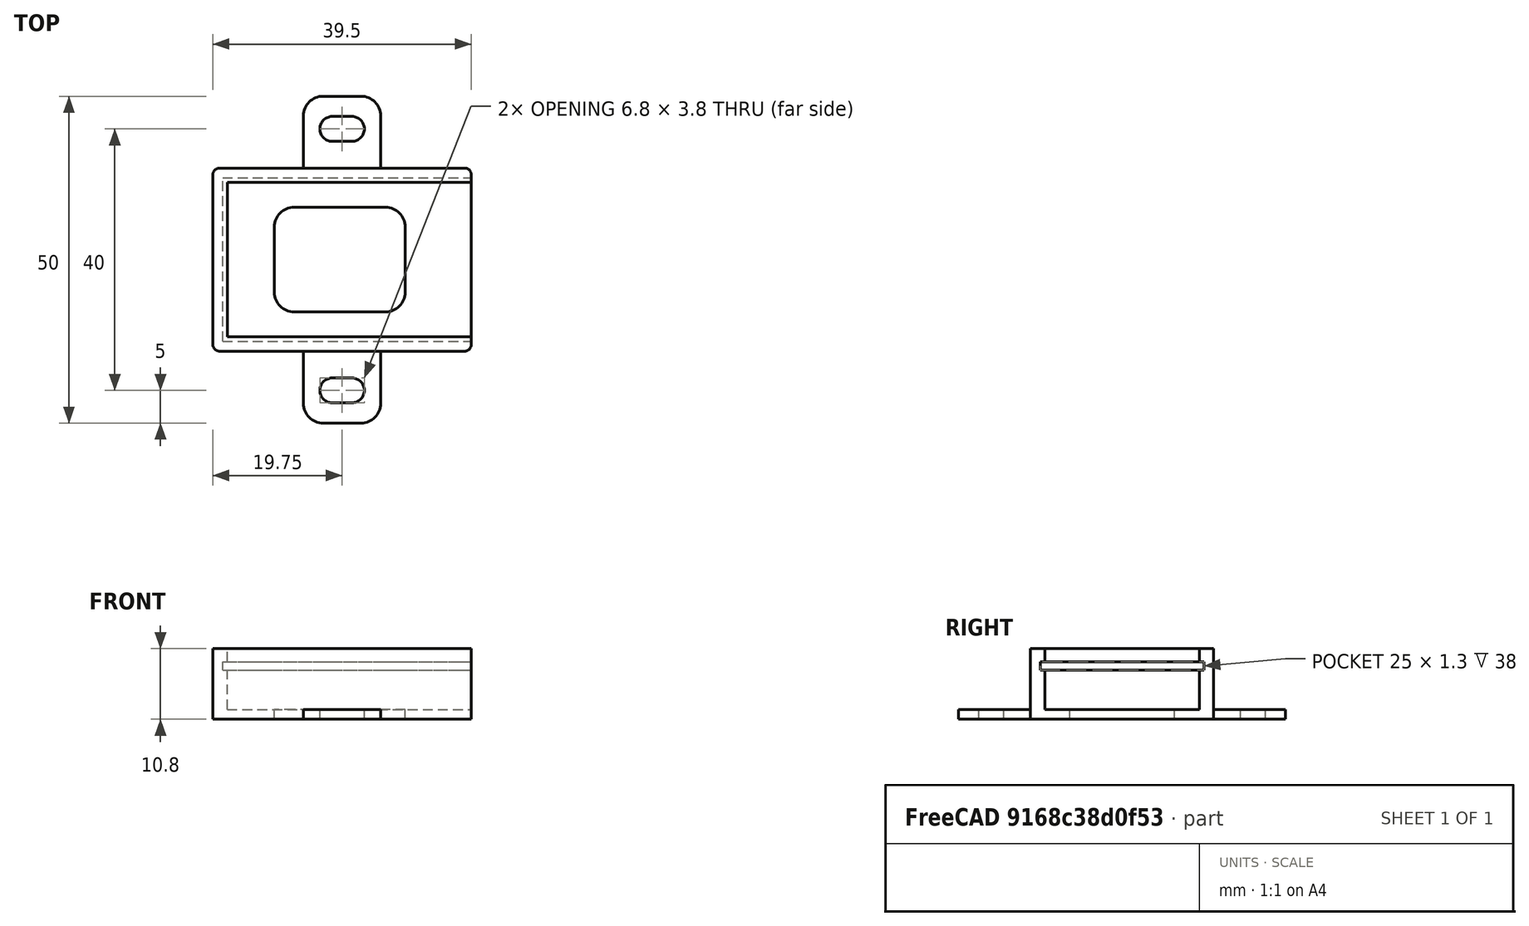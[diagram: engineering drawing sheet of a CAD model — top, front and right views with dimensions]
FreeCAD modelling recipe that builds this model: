
FCSTD DOCUMENT  (FreeCAD 0.19R23578 (Git))
Label: single_mosfet_30n06
License: FreeArt
LicenseURL: http://artlibre.org/licence/lal
objects: Part::Box×4, Part::Fillet×2, Part::MultiFuse×2, Spreadsheet::Sheet×1, Part::Feature×1, Part::Cut×1, App::Part×1
note: 10 computed .brp shape members not serialized (recipe doc carries the construction recipe); baked Part::Feature solids carry a one-line shape summary decoded from their .brp

FEATURE [Spreadsheet::Sheet] Spreadsheet  label="p"
  cells = A1=pcb_x; B1(pcb_x)=38; A2=pcb_y; B2(pcb_y)=25; A3=pcb_z; B3(pcb_z)=1.3; A4=pcb_under; B4(pcb_under)=6; A5=side_wall; B5(side_wall)=1.5; A6=pcb_side_lane; B6(pcb_side_lane)=0.7; A7=bottom_wall; B7(bottom_wall)=1.5; A8=pcb_above; B8(pcb_above)=2; A9=bottom_hole_x; B9(bottom_hole_x)=20; A10=bottom_hole_y; B10(bottom_hole_y)=16
FEATURE [Part::Box] Box  label="external cube"
  AttacherType = Attacher::AttachEngine3D
  Height = 10.8
  Length = 39.5
  Width = 28
  expr: Length = <<p>>.pcb_x + <<p>>.side_wall
  expr: Width = <<p>>.pcb_y + 2 * <<p>>.side_wall
  expr: Height = <<p>>.bottom_wall + <<p>>.pcb_under + <<p>>.pcb_z + <<p>>.pcb_above
FEATURE [Part::Box] Box006  label="internal cube"
  AttacherType = Attacher::AttachEngine3D
  Height = 9.3
  Length = 38.1
  Placement = pos=(2.2,2.2,1.5) rot=(0,0,1;0rad)
  Width = 23.6
  expr: Length = <<p>>.pcb_x - 2 * <<p>>.pcb_side_lane + <<p>>.side_wall
  expr: Width = <<p>>.pcb_y - 2 * <<p>>.pcb_side_lane
  expr: Height = <<p>>.pcb_under + <<p>>.pcb_z + <<p>>.pcb_above
  expr: .Placement.Base.z = <<p>>.bottom_wall
  expr: .Placement.Base.x = <<p>>.side_wall + <<p>>.pcb_side_lane
  expr: .Placement.Base.y = <<p>>.side_wall + <<p>>.pcb_side_lane
FEATURE [Part::Box] Box007  label="pcb extract cube"
  AttacherType = Attacher::AttachEngine3D
  Height = 1.3
  Length = 38
  Placement = pos=(1.5,1.5,7.5) rot=(0,0,1;0rad)
  Width = 25
  expr: Height = <<p>>.pcb_z
  expr: .Placement.Base.z = <<p>>.bottom_wall + <<p>>.pcb_under
  expr: Width = <<p>>.pcb_y
  expr: Length = <<p>>.pcb_x
  expr: .Placement.Base.x = <<p>>.side_wall
  expr: .Placement.Base.y = <<p>>.side_wall
FEATURE [Part::Fillet] Fillet  label="external fillet"
  Base = -> Box
  Edges = 4 edges r=1: [Edge1,Edge3,Edge5,Edge7]
FEATURE [Part::Box] Box008  label="bottom hole"
  AttacherType = Attacher::AttachEngine3D
  Height = 10
  Length = 20
  Placement = pos=(9.4,6,0) rot=(0,0,1;0rad)
  Width = 16
  expr: .Placement.Base.y = (<<p>>.pcb_y + 2 * <<p>>.side_wall - <<p>>.bottom_hole_y) / 2
  expr: .Placement.Base.x = (<<p>>.pcb_x + <<p>>.side_wall - <<p>>.pcb_side_lane - <<p>>.bottom_hole_x) / 2
  expr: Width = <<p>>.bottom_hole_y
  expr: Length = <<p>>.bottom_hole_x
FEATURE [Part::Fillet] Fillet001  label="bottom hole fillet"
  Base = -> Box008
  Edges = 4 edges r=3: [Edge1,Edge3,Edge5,Edge7]
FEATURE [Part::MultiFuse] Fusion  label="extract fusion"
  Shapes = -> [Box006,Box007,Fillet001]
FEATURE [Part::Feature] Cut002001  label="attach plane y dir001"
  Placement = pos=(13.85,-11,0) rot=(0,0,1;0rad)
  shape: bbox 11.8 x 50 x 1.5 mm, 20 faces (baked)
FEATURE [Part::MultiFuse] Fusion001  label="solid fusion"
  Shapes = -> [Fillet,Cut002001]
FEATURE [Part::Cut] Cut  label="body cut"
  Base = -> Fusion001
  Tool = -> Fusion
FEATURE [App::Part] Part  label="pcb box part"
  Group = -> [Box,Fillet,Fusion001,Fusion,Box007,Box006,Cut]
  Origin = -> Origin
